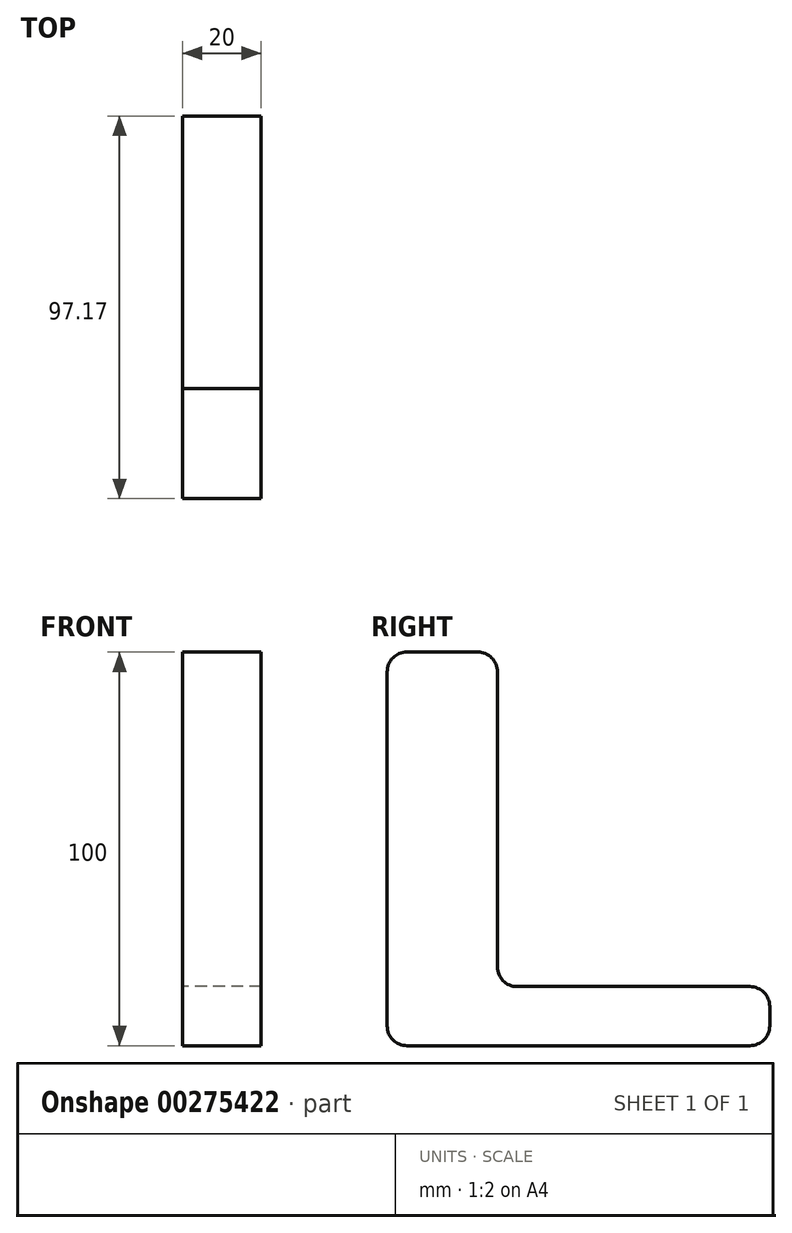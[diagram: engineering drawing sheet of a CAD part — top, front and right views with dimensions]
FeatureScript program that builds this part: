
annotation { "Feature Type Name" : "Feature", "Feature Type Description" : "" }
export const myFeature = defineFeature(function(context is Context, id is Id, definition is map)
    precondition{}
    {
        {
            var Q0;
            Q0=qCreatedBy(makeId("Right.planeOp"),FACE);
            var sketch = newSketch(context, id + "F0", { "sketchPlane" : qUnion([Q0])});
            skLineSegment(sketch, "E0", {"start": v(-48.75, 39.78) * mm, "end": v(-30.75, 39.78) * mm});
            skLineSegment(sketch, "E1", {"start": v(-25.75, 34.78) * mm, "end": v(-25.75, -40.22) * mm});
            skLineSegment(sketch, "E2", {"start": v(-20.75, -45.22) * mm, "end": v(38.42, -45.22) * mm});
            skLineSegment(sketch, "E3", {"start": v(43.42, -50.22) * mm, "end": v(43.42, -55.22) * mm});
            skLineSegment(sketch, "E4", {"start": v(38.42, -60.22) * mm, "end": v(-48.75, -60.22) * mm});
            skLineSegment(sketch, "E5", {"start": v(-53.75, -55.22) * mm, "end": v(-53.75, 34.78) * mm});
            skPoint(sketch, "E6.visualSharp", {"position": v(-53.75, 39.78) * mm});
            skArc(sketch, "E6.filletArc", {"start": v(-48.75, 39.78) * mm, "mid": v(-52.28, 38.32) * mm, "end": v(-53.75, 34.78) * mm});
            skPoint(sketch, "E7.visualSharp", {"position": v(-25.75, 39.78) * mm});
            skArc(sketch, "E7.filletArc", {"start": v(-25.75, 34.78) * mm, "mid": v(-27.21, 38.32) * mm, "end": v(-30.75, 39.78) * mm});
            skPoint(sketch, "E8.visualSharp", {"position": v(-53.75, -60.22) * mm});
            skArc(sketch, "E8.filletArc", {"start": v(-53.75, -55.22) * mm, "mid": v(-52.28, -58.75) * mm, "end": v(-48.75, -60.22) * mm});
            skPoint(sketch, "E9.visualSharp", {"position": v(-25.75, -45.22) * mm});
            skArc(sketch, "E9.filletArc", {"start": v(-25.75, -40.22) * mm, "mid": v(-24.28, -43.75) * mm, "end": v(-20.75, -45.22) * mm});
            skPoint(sketch, "E10.visualSharp", {"position": v(43.42, -45.22) * mm});
            skArc(sketch, "E10.filletArc", {"start": v(43.42, -50.22) * mm, "mid": v(41.95, -46.68) * mm, "end": v(38.42, -45.22) * mm});
            skPoint(sketch, "E11.visualSharp", {"position": v(43.42, -60.22) * mm});
            skArc(sketch, "E11.filletArc", {"start": v(38.42, -60.22) * mm, "mid": v(41.95, -58.75) * mm, "end": v(43.42, -55.22) * mm});
            skSolve(sketch);
        }
        {
            var Q0;
            Q0=makeQuery(id+"F0.imprint","IMPRINT",FACE,{"disambiguationData":[TD([[makeQuery(id+"F0.imprint","IMPRINT",EDGE,{"derivedFrom":sQuery(id+"F0.wireOp",EDGE,"E0")}),-1.0]])]});
            extrude(context, id + "F1", {"entities" : qUnion([Q0]), "depth" : 20 * mm});
        }
    });
